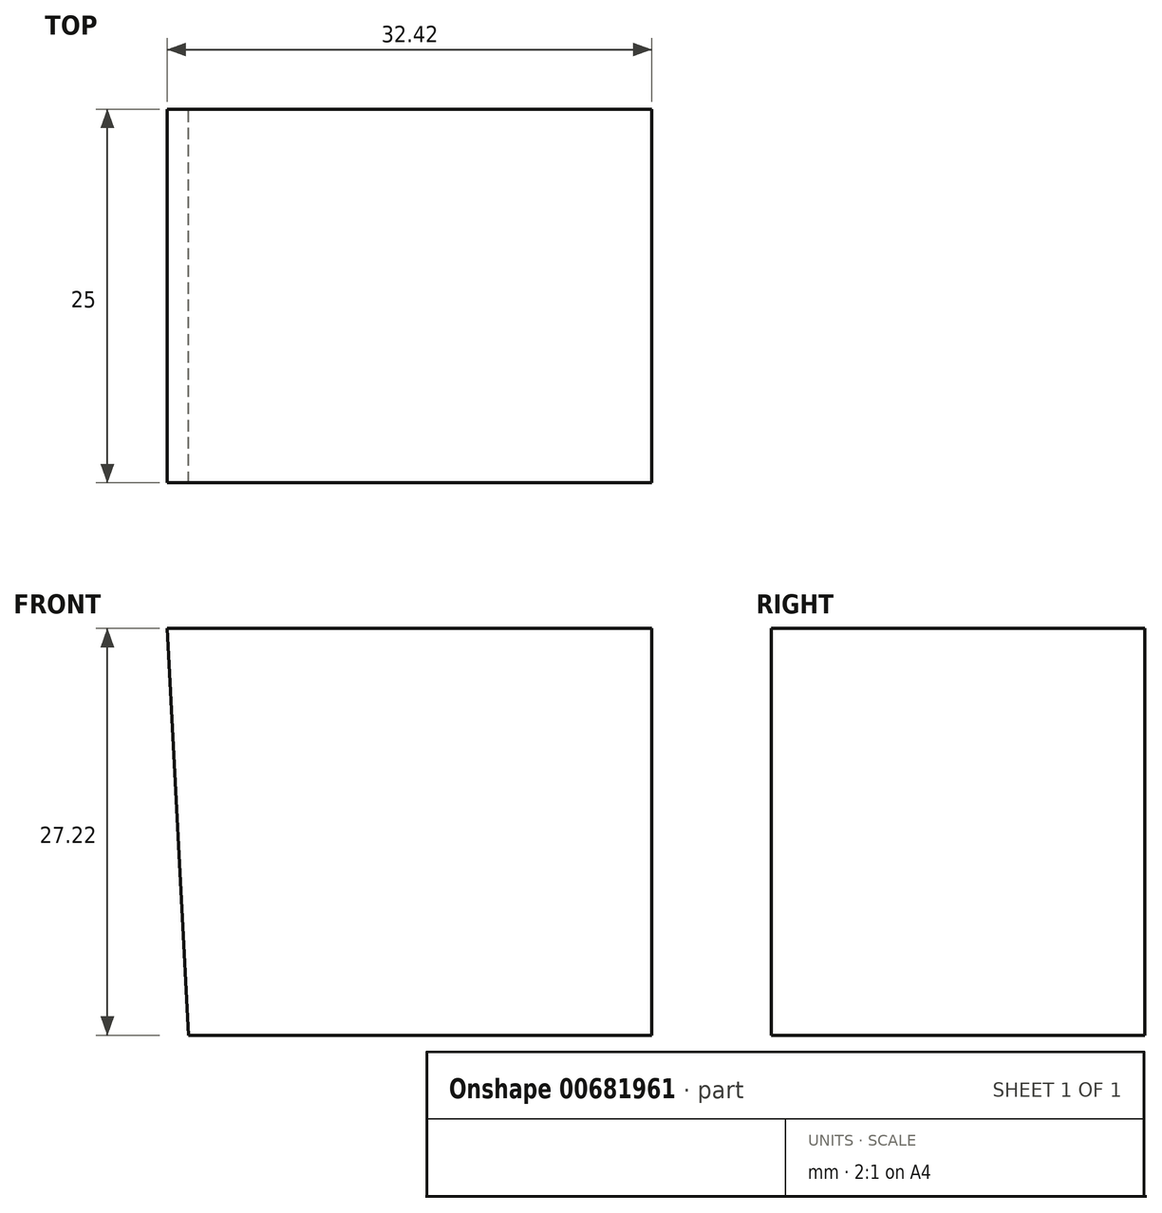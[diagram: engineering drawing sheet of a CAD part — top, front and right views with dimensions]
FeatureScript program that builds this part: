
annotation { "Feature Type Name" : "Feature", "Feature Type Description" : "" }
export const myFeature = defineFeature(function(context is Context, id is Id, definition is map)
    precondition{}
    {
        {
            var Q0;
            Q0=qCreatedBy(makeId("Front.planeOp"),FACE);
            var sketch = newSketch(context, id + "F0", { "sketchPlane" : qUnion([Q0])});
            skLineSegment(sketch, "E0", {"start": v(-57.61, 54.29) * mm, "end": v(-25.19, 54.29) * mm});
            skLineSegment(sketch, "E1", {"start": v(-25.19, 54.29) * mm, "end": v(-25.19, 27.07) * mm});
            skLineSegment(sketch, "E2", {"start": v(-25.19, 27.07) * mm, "end": v(-56.17, 27.07) * mm});
            skLineSegment(sketch, "E3", {"start": v(-56.17, 27.07) * mm, "end": v(-57.61, 54.29) * mm});
            skSolve(sketch);
        }
        {
            var Q0;
            Q0=makeQuery(id+"F0.imprint","IMPRINT",FACE,{"disambiguationData":[TD([[makeQuery(id+"F0.imprint","IMPRINT",EDGE,{"derivedFrom":sQuery(id+"F0.wireOp",EDGE,"E0")}),-1.0]])]});
            extrude(context, id + "F1", {"entities" : qUnion([Q0]), "depth" : 25 * mm, "offsetDistance" : 25 * mm});
        }
    });
